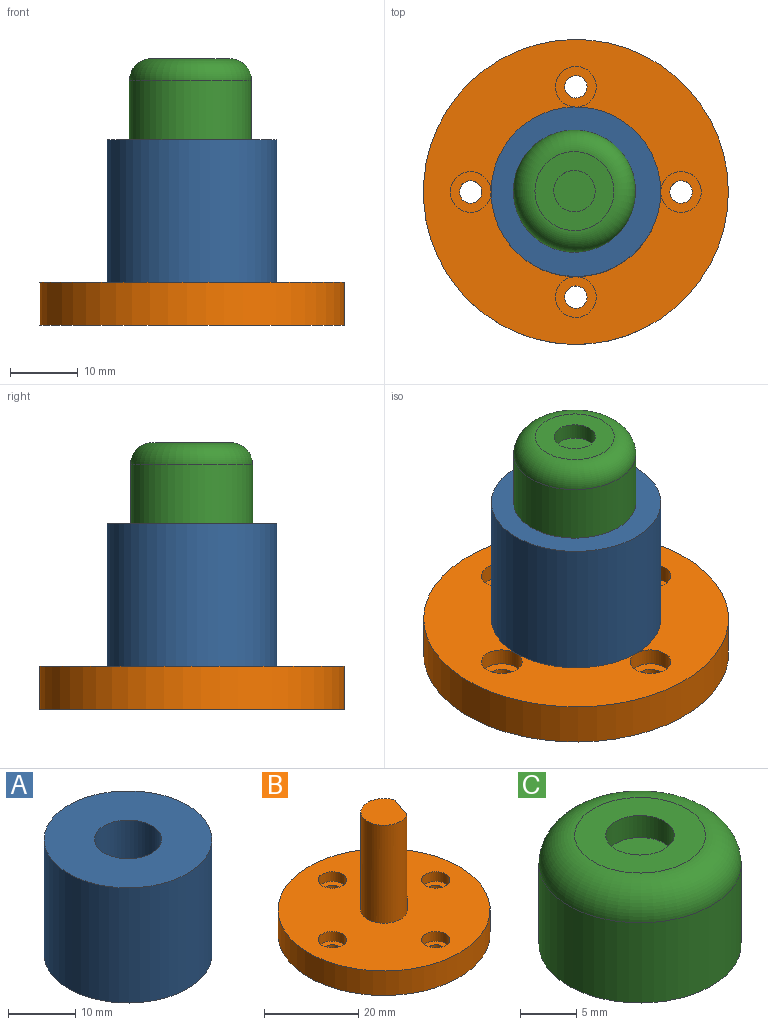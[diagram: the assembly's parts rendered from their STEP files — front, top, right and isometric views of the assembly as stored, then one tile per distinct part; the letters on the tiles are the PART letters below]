
ASSEMBLY  parts=3 mates=5
PART A: 4 faces, bbox 25x25x21 mm
  f0: cylinder r=5mm len=21mm, axis (0,0,-1), area 659.7mm2, adj f2,f3
  f1: cylinder r=12.5mm len=25mm, axis (0,0,-1), area 1649.3mm2, adj f2,f3
  f2: plane 25x25mm, normal (0,0,1), area 412.3mm2, adj f0,f1
  f3: plane 25x25mm, normal (0,0,-1), area 412.3mm2, adj f0,f1
PART B: 21 faces, bbox 45x45x31.8 mm
  f0: cylinder r=1.65mm len=3.85mm, axis (0,0,-1), area 39.9mm2, adj f7,f20
  f1: cylinder r=1.65mm len=3.85mm, axis (0,0,-1), area 39.9mm2, adj f7,f18
  f2: cylinder r=1.65mm len=3.85mm, axis (0,0,-1), area 39.9mm2, adj f7,f16
  f3: cylinder r=1.65mm len=3.85mm, axis (0,0,-1), area 39.9mm2, adj f7,f14
  f4: plane 9.85x9.64mm, normal (0,0,1), area 72.6mm2, adj f8,f11
  f5: cylinder r=22.48mm len=44.96mm, axis (0,0,-1), area 896.9mm2, adj f6,f7
  f6: plane 44.96x44.96mm, normal (0,0,1), area 1398.2mm2, adj f5,f8,f13,f15,f17,f19
  f7: plane 44.96x44.96mm, normal (0,0,-1), area 1540.7mm2, adj f0,f1,f2,f3,f5,f9
  f8: cylinder r=4.92mm len=25.4mm, axis (0,0,-1), area 649.6mm2, adj f4,f6,f11,f12
  f9: cylinder r=2mm len=7mm, axis (0,0,-1), area 88mm2, adj f7,f10
  f10: plane 4x4mm, normal (0,0,-1), area 12.6mm2, adj f9
  f11: plane 22.23x5.44mm, normal (0.95,-0.32,0), area 127.7mm2, adj f4,f8,f12
  f12: plane 5.44x2.07mm, normal (0,0,1), area 3.6mm2, adj f8,f11
  f13: cylinder r=3mm len=6mm, axis (0,0,1), area 47.1mm2, adj f6,f14
  f14: plane 6x6mm, normal (0,0,1), area 19.7mm2, adj f3,f13
  f15: cylinder r=3mm len=6mm, axis (0,0,1), area 47.1mm2, adj f6,f16
  f16: plane 6x6mm, normal (0,0,1), area 19.7mm2, adj f2,f15
  f17: cylinder r=3mm len=6mm, axis (0,0,1), area 47.1mm2, adj f6,f18
  f18: plane 6x6mm, normal (0,0,1), area 19.7mm2, adj f1,f17
  f19: cylinder r=3mm len=6mm, axis (0,0,1), area 47.1mm2, adj f6,f20
  f20: plane 6x6mm, normal (0,0,1), area 19.7mm2, adj f0,f19
PART C: 9 faces, bbox 19.5x19.5x11.9 mm
  f0: cylinder r=5mm len=10mm, axis (0,0,-1), area 158.6mm2, adj f1,f3,f4
  f1: plane 6.35x6mm, normal (-1,0,0), area 38.1mm2, adj f0,f3,f4
  f2: cylinder r=9mm len=18mm, axis (0,0,-1), area 494.8mm2, adj f3,f8
  f3: plane 18x18mm, normal (0,0,-1), area 180mm2, adj f0,f1,f2
  f4: plane 10x9mm, normal (0,0,-1), area 74.5mm2, adj f0,f1
  f5: cylinder r=3.05mm len=6.1mm, axis (0,0,-1), area 46mm2, adj f6,f7
  f6: plane 11.65x11.65mm, normal (0,0,1), area 77.4mm2, adj f5,f8
  f7: plane 6.1x6.1mm, normal (0,0,1), area 29.2mm2, adj f5
  f8: torus R=5.83mm, axis (0,0,1), area 245.9mm2, adj f2,f6
PLACE A rot(axis=(1,0,0),180deg) t=(-24.08,9.01,16.09)mm
PLACE B t=(-24.08,9.01,-11.26)mm
PLACE C rot(axis=(0,0,-1),18.9deg) t=(-24.28,9.08,16.09)mm
MATE cylindrical C.f0 <-> B.f4  axis (0,0,-1) through (-24.28,9.08,16.09)mm
MATE cylindrical A.f0 <-> B.f5  axis (0,0,-1) through (-24.08,9.01,-4.91)mm
MATE planar A.f1 <-> B.f5  axis (0,0,-1) through (-24.08,9.01,-4.91)mm
MATE parallel C.f1 <-> B.f11  axis (-0.95,0.32,0) through (-20.5,7.79,19.26)mm
MATE planar C.f3 <-> A.f1  axis (0,0,-1) through (-24.19,9.05,16.09)mm
